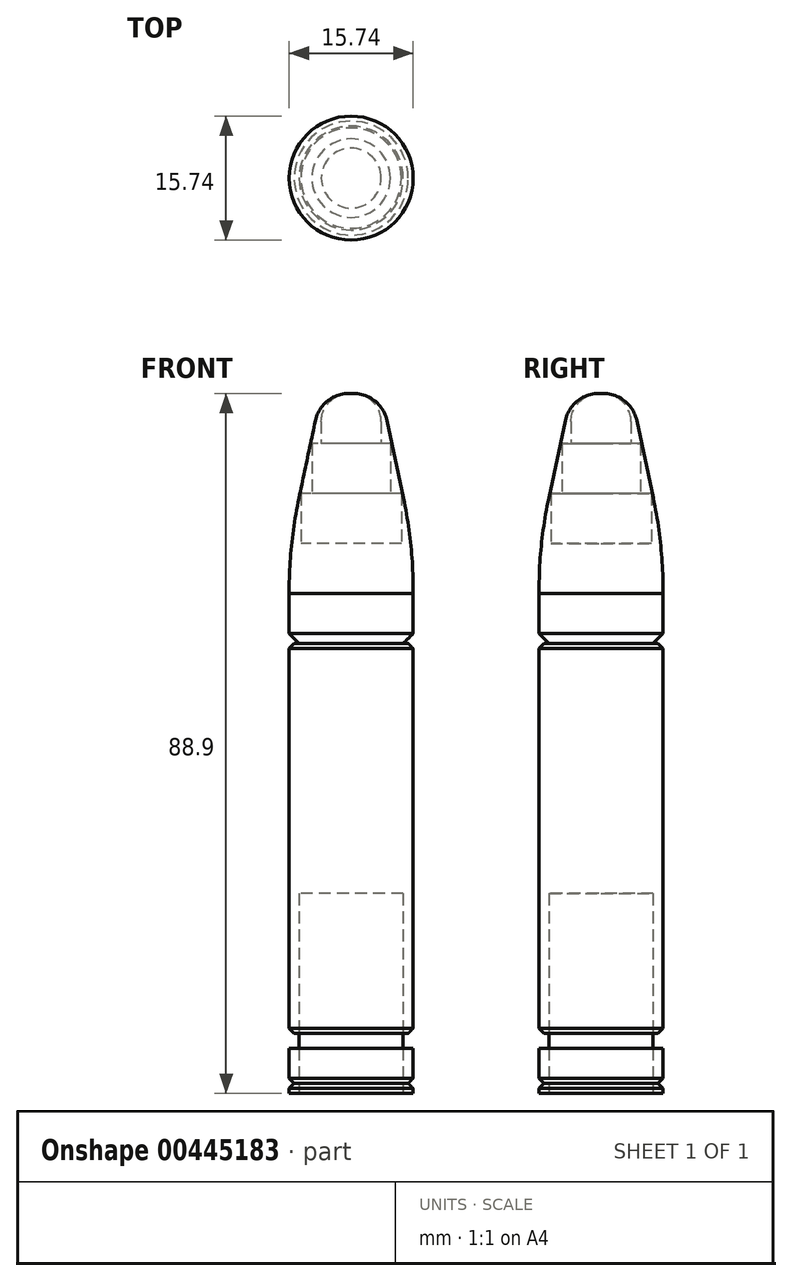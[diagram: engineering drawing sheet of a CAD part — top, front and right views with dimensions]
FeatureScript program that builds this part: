
annotation { "Feature Type Name" : "Feature", "Feature Type Description" : "" }
export const myFeature = defineFeature(function(context is Context, id is Id, definition is map)
    precondition{}
    {
        {
            var Q0;
            Q0=qCreatedBy(makeId("Top.planeOp"),FACE);
            var sketch = newSketch(context, id + "F0", { "sketchPlane" : qUnion([Q0])});
            skCircle(sketch, "E0", {"center": v(0, 0) * mm, "radius": 7.87 * mm});
            skCircle(sketch, "E1.0", {"center": v(0, 0) * mm, "radius": 6.6 * mm});
            skSolve(sketch);
        }
        {
            var Q0;
            Q0=makeQuery(id+"F0.imprint","IMPRINT",FACE,{"disambiguationData":[TD([[makeQuery(id+"F0.imprint","IMPRINT",EDGE,{"derivedFrom":sQuery(id+"F0.wireOp",EDGE,"E0")}),1.0]])]});
            var Q1;
            Q1=makeQuery(id+"F0.imprint","IMPRINT",FACE,{"disambiguationData":[TD([[makeQuery(id+"F0.imprint","IMPRINT",EDGE,{"derivedFrom":sQuery(id+"F0.wireOp",EDGE,"E1.0")}),1.0]])]});
            extrude(context, id + "F1", {"entities" : qUnion([Q0, Q1]), "depth" : 5.7 * mm, "hasSecondDirection" : true, "secondDirectionOppositeDirection" : true, "secondDirectionDepth" : -1.27 * mm});
        }
        {
            var Q0;
            Q0=makeQuery(id+"F0.imprint","IMPRINT",FACE,{"disambiguationData":[TD([[makeQuery(id+"F0.imprint","IMPRINT",EDGE,{"derivedFrom":sQuery(id+"F0.wireOp",EDGE,"E0")}),1.0]])]});
            var Q1;
            Q1=makeQuery(id+"F0.imprint","IMPRINT",FACE,{"disambiguationData":[TD([[makeQuery(id+"F0.imprint","IMPRINT",EDGE,{"derivedFrom":sQuery(id+"F0.wireOp",EDGE,"E1.0")}),1.0]])]});
            extrude(context, id + "F2", {"entities" : qUnion([Q0, Q1]), "depth" : 57.15 * mm, "hasSecondDirection" : true, "secondDirectionOppositeDirection" : true, "secondDirectionDepth" : -7.62 * mm});
        }
        {
            var Q0;
            Q0=makeQuery(id+"F2.opExtrude","CAP_FACE",FACE,{"disambiguationData":[OSD([sQuery(id+"F0.wireOp",EDGE,"E0")])],"isStart":false});
            var sketch = newSketch(context, id + "F3", { "sketchPlane" : qUnion([Q0])});
            skSolve(sketch);
        }
        {
            var Q0;
            Q0=makeQuery(id+"F0.imprint","IMPRINT",FACE,{"disambiguationData":[TD([[makeQuery(id+"F0.imprint","IMPRINT",EDGE,{"derivedFrom":sQuery(id+"F0.wireOp",EDGE,"E1.0")}),1.0]])]});
            extrude(context, id + "F4", {"entities" : qUnion([Q0]), "depth" : 25.4 * mm});
        }
        {
            var Q0;
            Q0=makeQuery(id+"F3.imprint","IMPRINT",FACE,{"disambiguationData":[TD([[makeQuery(id+"F3.imprint","IMPRINT",EDGE,{"derivedFrom":makeQuery(id+"F2.opExtrude","CAP_EDGE",EDGE,{"disambiguationData":[OSD([sQuery(id+"F0.wireOp",EDGE,"E0")])],"isStart":false})}),1.0]])]});
            extrude(context, id + "F5", {"entities" : qUnion([Q0]), "depth" : 6.35 * mm, "hasSecondDirection" : true, "secondDirectionOppositeDirection" : true, "secondDirectionDepth" : 0 * mm});
        }
        {
            var Q0;
            Q0=makeQuery(id+"F5.opExtrude","CAP_FACE",FACE,{"disambiguationData":[OSD([sQuery(id+"F0.wireOp",EDGE,"E0")])],"isStart":false});
            var sketch = newSketch(context, id + "F6", { "sketchPlane" : qUnion([Q0])});
            skSolve(sketch);
        }
        {
            var Q0;
            Q0=makeQuery(id+"F6.imprint","IMPRINT",FACE,{"disambiguationData":[TD([[makeQuery(id+"F6.imprint","IMPRINT",EDGE,{"derivedFrom":makeQuery(id+"F5.opExtrude","CAP_EDGE",EDGE,{"disambiguationData":[OSD([sQuery(id+"F0.wireOp",EDGE,"E0")])],"isStart":false})}),1.0]])]});
            extrude(context, id + "F7", {"entities" : qUnion([Q0]), "depth" : 6.35 * mm});
        }
        {
            var Q0;
            Q0=makeQuery(id+"F7.opExtrude","CAP_FACE",FACE,{"disambiguationData":[OSD([sQuery(id+"F0.wireOp",EDGE,"E0")])],"isStart":false});
            var sketch = newSketch(context, id + "F8", { "sketchPlane" : qUnion([Q0])});
            skCircle(sketch, "E2", {"center": v(0, 0) * mm, "radius": 6.38 * mm});
            skSolve(sketch);
        }
        {
            var Q0;
            Q0=makeQuery(id+"F8.imprint","IMPRINT",FACE,{"disambiguationData":[TD([[makeQuery(id+"F8.imprint","IMPRINT",EDGE,{"derivedFrom":sQuery(id+"F8.wireOp",EDGE,"E2")}),1.0]])]});
            extrude(context, id + "F9", {"entities" : qUnion([Q0]), "depth" : 6.35 * mm});
        }
        {
            var Q0;
            Q0=makeQuery(id+"F9.opExtrude","CAP_FACE",FACE,{"disambiguationData":[OSD([sQuery(id+"F8.wireOp",EDGE,"E2")])],"isStart":false});
            var sketch = newSketch(context, id + "F10", { "sketchPlane" : qUnion([Q0])});
            skCircle(sketch, "E3", {"center": v(0, 0) * mm, "radius": 5 * mm});
            skSolve(sketch);
        }
        {
            var Q0;
            Q0=makeQuery(id+"F10.imprint","IMPRINT",FACE,{"disambiguationData":[TD([[makeQuery(id+"F10.imprint","IMPRINT",EDGE,{"derivedFrom":sQuery(id+"F10.wireOp",EDGE,"E3")}),1.0]])]});
            extrude(context, id + "F11", {"entities" : qUnion([Q0]), "depth" : 6.35 * mm});
        }
        {
            var Q0;
            Q0=makeQuery(id+"F11.opExtrude","CAP_FACE",FACE,{"disambiguationData":[OSD([sQuery(id+"F10.wireOp",EDGE,"E3")])],"isStart":false});
            var sketch = newSketch(context, id + "F12", { "sketchPlane" : qUnion([Q0])});
            skCircle(sketch, "E4", {"center": v(0, 0) * mm, "radius": 3.8 * mm});
            skSolve(sketch);
        }
        {
            var Q0;
            Q0 = qSketchRegion(id + "F12", true);
            extrude(context, id + "F13", {"entities" : qUnion([Q0]), "depth" : 6.35 * mm});
        }
        {
            var Q0;
            Q0=makeQuery(id+"F7.opExtrude","CAP_FACE",FACE,{"disambiguationData":[OSD([sQuery(id+"F0.wireOp",EDGE,"E0")])],"isStart":false});
            var Q1;
            Q1=makeQuery(id+"F13.opExtrude","CAP_FACE",FACE,{"disambiguationData":[OSD([sQuery(id+"F12.wireOp",EDGE,"E4")])],"isStart":false});
            loft(context, id + "F14", {"sheetProfilesArray" : [{ "sheetProfileEntities" : qUnion([Q0]) }, { "sheetProfileEntities" : qUnion([Q1]) }]});
        }
        {
            var Q0;
            Q0=makeQuery(id+"F7.opExtrude","SWEPT_BODY",BODY,{"disambiguationData":[OSD([sQuery(id+"F0.wireOp",EDGE,"E0")])]});
            var Q1;
            Q1=makeQuery(id+"F14.opLoft","SWEPT_BODY",BODY,{"disambiguationData":[OSD([sQuery(id+"F0.wireOp",EDGE,"E0"),sQuery(id+"F12.wireOp",EDGE,"E4")])]});
            booleanBodies(context, id + "F15", {"operationType" : BooleanOperationType.UNION, "tools" : qUnion([Q0, Q1])});
        }
        {
            var Q0;
            {var subQ0=sQuery(id+"F0.wireOp",EDGE,"E0");Q0=makeQuery(id+"F15.opBoolean","MERGE",EDGE,{"derivedFrom":[makeQuery(id+"F7.opExtrude","CAP_EDGE",EDGE,{"disambiguationData":[OSD([subQ0])],"isStart":false}),makeQuery(id+"F14.opLoft","MID_CAP_EDGE",EDGE,{"disambiguationData":[OSD([subQ0])],"capPos":0.0})]});}
            fillet(context, id + "F16", {"entities" : qUnion([Q0]), "radius" : 55.88 * mm, "tangentPropagation" : true, "allowEdgeOverflow" : false});
        }
        {
            var Q0;
            Q0=makeQuery(id+"F13.opExtrude","CAP_EDGE",EDGE,{"disambiguationData":[OSD([sQuery(id+"F12.wireOp",EDGE,"E4")])],"isStart":false});
            fillet(context, id + "F17", {"entities" : qUnion([Q0]), "radius" : 3.56 * mm, "tangentPropagation" : true, "allowEdgeOverflow" : false});
        }
        {
            var Q0;
            Q0=makeQuery(id+"F14.opLoft","MID_CAP_EDGE",EDGE,{"disambiguationData":[OSD([sQuery(id+"F0.wireOp",EDGE,"E0"),sQuery(id+"F12.wireOp",EDGE,"E4")])],"capPos":1.0});
            fillet(context, id + "F18", {"entities" : qUnion([Q0]), "radius" : 4.32 * mm, "tangentPropagation" : true, "allowEdgeOverflow" : false});
        }
        {
            var Q0;
            Q0=makeQuery(id+"F2.opExtrude","CAP_EDGE",EDGE,{"disambiguationData":[OSD([sQuery(id+"F0.wireOp",EDGE,"E0")])],"isStart":false});
            chamfer(context, id + "F19", {"entities" : qUnion([Q0]), "width" : 0.64 * mm, "tangentPropagation" : true});
        }
        {
            var Q0;
            Q0=makeQuery(id+"F5.opExtrude","CAP_EDGE",EDGE,{"disambiguationData":[OSD([sQuery(id+"F0.wireOp",EDGE,"E0")])],"isStart":true});
            chamfer(context, id + "F20", {"entities" : qUnion([Q0]), "width" : 1.27 * mm, "tangentPropagation" : true});
        }
        {
            var Q0;
            Q0=makeQuery(id+"F0.imprint","IMPRINT",FACE,{"disambiguationData":[TD([[makeQuery(id+"F0.imprint","IMPRINT",EDGE,{"derivedFrom":sQuery(id+"F0.wireOp",EDGE,"E0")}),1.0]])]});
            var Q1;
            Q1=makeQuery(id+"F0.imprint","IMPRINT",FACE,{"disambiguationData":[TD([[makeQuery(id+"F0.imprint","IMPRINT",EDGE,{"derivedFrom":sQuery(id+"F0.wireOp",EDGE,"E1.0")}),1.0]])]});
            extrude(context, id + "F21", {"entities" : qUnion([Q0, Q1]), "depth" : 1.27 * mm});
        }
        {
            var Q0;
            Q0=makeQuery(id+"F1.opExtrude","CAP_EDGE",EDGE,{"disambiguationData":[OSD([sQuery(id+"F0.wireOp",EDGE,"E0")])],"isStart":true});
            chamfer(context, id + "F22", {"entities" : qUnion([Q0]), "width" : 0.64 * mm, "tangentPropagation" : true});
        }
        {
            var Q0;
            Q0=makeQuery(id+"F21.opExtrude","CAP_EDGE",EDGE,{"disambiguationData":[OSD([sQuery(id+"F0.wireOp",EDGE,"E0")])],"isStart":false});
            chamfer(context, id + "F23", {"entities" : qUnion([Q0]), "width" : 0.64 * mm, "tangentPropagation" : true});
        }
        {
            var Q0;
            Q0=makeQuery(id+"F2.opExtrude","CAP_EDGE",EDGE,{"disambiguationData":[OSD([sQuery(id+"F0.wireOp",EDGE,"E0")])],"isStart":true});
            chamfer(context, id + "F24", {"entities" : qUnion([Q0]), "width" : 0.64 * mm, "tangentPropagation" : true});
        }
    });
